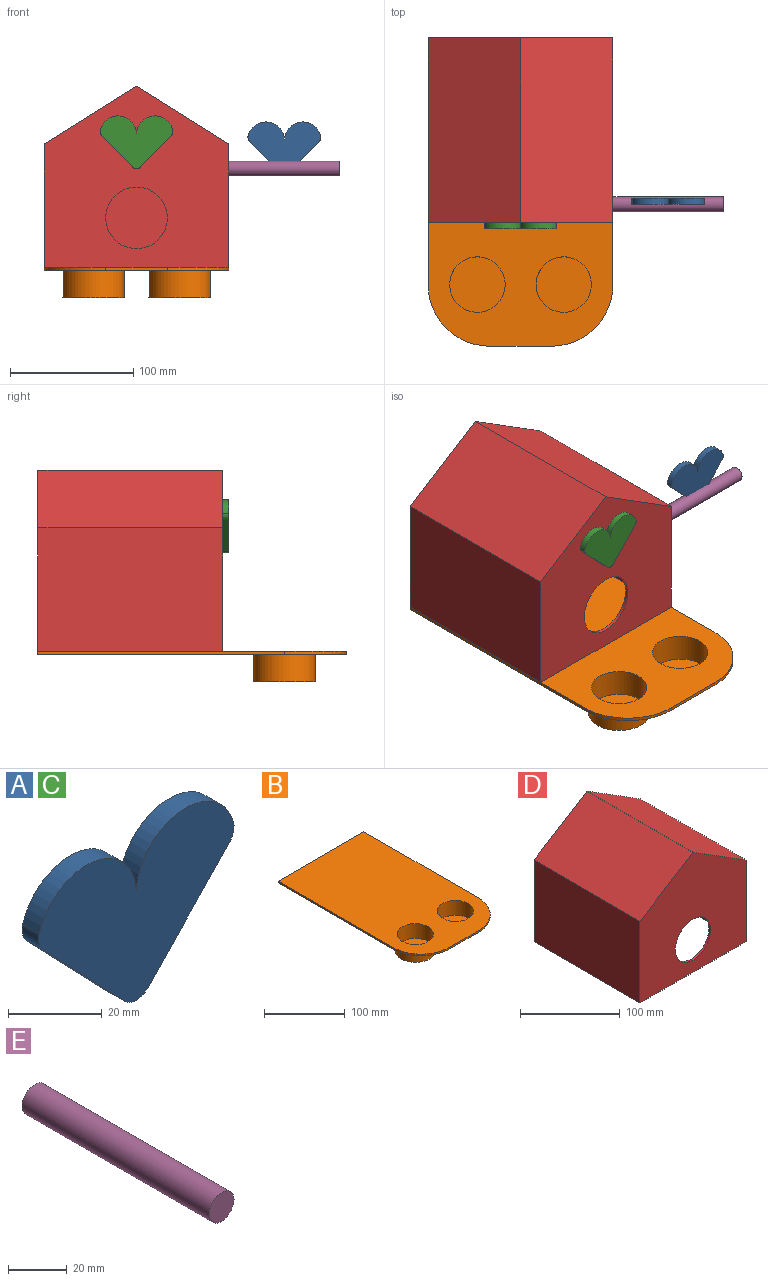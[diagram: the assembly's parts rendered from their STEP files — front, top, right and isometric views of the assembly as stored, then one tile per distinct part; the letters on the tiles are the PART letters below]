
ASSEMBLY  parts=5 mates=4
PART A: 9 faces, bbox 59.1x5x42.9 mm
  f0: plane 25.61x24.57mm, normal (0.72,0,-0.69), area 177.5mm2, adj f2,f3,f7,f8
  f1: cylinder r=15mm len=29.38mm, axis (0,1,0), area 209.1mm2, adj f2,f3,f5,f7
  f2: plane 59.14x42.85mm, normal (0,-1,0), area 1565.2mm2, adj f0,f1,f4,f5,f6,f7,f8
  f3: plane 59.14x42.85mm, normal (0,1,0), area 1565.2mm2, adj f0,f1,f4,f5,f6,f7,f8
  f4: plane 25.61x24.57mm, normal (-0.72,0,-0.69), area 177.5mm2, adj f2,f3,f6,f8
  f5: cylinder r=15mm len=29.38mm, axis (0,1,0), area 209.1mm2, adj f1,f2,f3,f6
  f6: cylinder r=5mm len=5mm, axis (0,1,0), area 26.1mm2, adj f2,f3,f4,f5
  f7: cylinder r=5mm len=5mm, axis (0,1,0), area 26.1mm2, adj f0,f1,f2,f3
  f8: cylinder r=5mm len=7.22mm, axis (0,1,0), area 40.3mm2, adj f0,f2,f3,f4
PART B: 16 faces, bbox 150x250x25 mm
  f0: plane 200x2.5mm, normal (1,0,0), area 500mm2, adj f1,f4,f5,f7
  f1: plane 150x2.5mm, normal (0,1,0), area 375mm2, adj f0,f2,f4,f5
  f2: plane 200x2.5mm, normal (-1,0,0), area 500mm2, adj f1,f4,f5,f6
  f3: plane 50x2.5mm, normal (0,-1,0), area 125mm2, adj f4,f5,f6,f7
  f4: plane 250x150mm, normal (0,0,1), area 33246.1mm2, adj f0,f1,f2,f3,f6,f7,f13,f14
  f5: plane 250x150mm, normal (0,0,-1), area 32500mm2, adj f0,f1,f2,f3,f6,f7,f8,f10
  f6: cylinder r=50mm len=50mm, axis (0,0,1), area 196.3mm2, adj f2,f3,f4,f5
  f7: cylinder r=50mm len=50mm, axis (0,0,-1), area 196.3mm2, adj f0,f3,f4,f5
  f8: cylinder r=25mm len=50mm, axis (0,0,1), area 3534.3mm2, adj f5,f9
  f9: plane 50x50mm, normal (0,0,-1), area 1963.5mm2, adj f8
  f10: cylinder r=25mm len=50mm, axis (0,0,1), area 3534.3mm2, adj f5,f11
  f11: plane 50x50mm, normal (0,0,-1), area 1963.5mm2, adj f10
  f12: plane 45x45mm, normal (0,0,1), area 1590.4mm2, adj f13
  f13: cylinder r=22.5mm len=45mm, axis (0,0,1), area 3180.9mm2, adj f4,f12
  f14: cylinder r=22.5mm len=45mm, axis (0,0,1), area 3180.9mm2, adj f4,f15
  f15: plane 45x45mm, normal (0,0,1), area 1590.4mm2, adj f14
PART C: same geometry as A
PART D: 14 faces, bbox 150x150x147 mm
  f0: plane 150x150mm, normal (0,0,-1), area 1475mm2, adj f1,f2,f5,f6,f7,f8,f11,f12
  f1: plane 150x100mm, normal (-1,0,0), area 15000mm2, adj f0,f4,f5,f6
  f2: plane 150x100mm, normal (1,0,0), area 15000mm2, adj f0,f3,f5,f6
  f3: plane 150x75mm, normal (0.53,0,0.85), area 13277.7mm2, adj f2,f4,f5,f6
  f4: plane 150x75mm, normal (-0.53,0,0.85), area 13277.7mm2, adj f1,f3,f5,f6
  f5: plane 150x147.01mm, normal (0,-1,0), area 16562.6mm2, adj f0,f1,f2,f3,f4,f13
  f6: plane 150x147.01mm, normal (0,1,0), area 18526.1mm2, adj f0,f1,f2,f3,f4
  f7: plane 145x98.62mm, normal (1,0,0), area 14299.4mm2, adj f0,f10,f11,f12
  f8: plane 145x98.62mm, normal (-1,0,0), area 14299.4mm2, adj f0,f9,f11,f12
  f9: plane 145x72.5mm, normal (-0.53,0,-0.85), area 12407.2mm2, adj f8,f10,f11,f12
  f10: plane 145x72.5mm, normal (0.53,0,-0.85), area 12407.2mm2, adj f7,f9,f11,f12
  f11: plane 145x144.06mm, normal (0,1,0), area 15630.9mm2, adj f0,f7,f8,f9,f10,f13
  f12: plane 145x144.06mm, normal (0,-1,0), area 17594.4mm2, adj f0,f7,f8,f9,f10
  f13: cylinder r=25mm len=50mm, axis (0,-1,0), area 392.7mm2, adj f5,f11
PART E: 3 faces, bbox 12x90x12 mm
  f0: cylinder r=6mm len=90mm, axis (0,-1,0), area 3392.9mm2, adj f1,f2
  f1: plane 12x12mm, normal (0,1,0), area 113.1mm2, adj f0
  f2: plane 12x12mm, normal (0,-1,0), area 113.1mm2, adj f0
PLACE A rot(axis=(0,0,1),180deg) t=(-8.67,-85.42,112.64)mm
PLACE B t=(-128.67,-75.42,6.17)mm
PLACE C rot(axis=(0,0,1),180deg) t=(-128.67,-105.42,117.53)mm
PLACE D t=(-203.67,49.58,8.67)mm
PLACE E rot(axis=(-0.58,0.58,0.58),120deg) t=(36.33,-85.42,88.67)mm
MATE fastened B.f4 <-> D.f0  axis (0,0,1) through (-53.67,49.58,8.67)mm
MATE ball E.f0 <-> A.f8  axis (1,0,0) through (-8.67,-85.42,88.67)mm
MATE fastened C.f2 <-> D.f5  axis (0,1,0) through (-128.67,-100.42,113.84)mm
MATE fastened E.f0 <-> D.f2  axis (-1,0,0) through (-53.67,-85.42,88.67)mm
